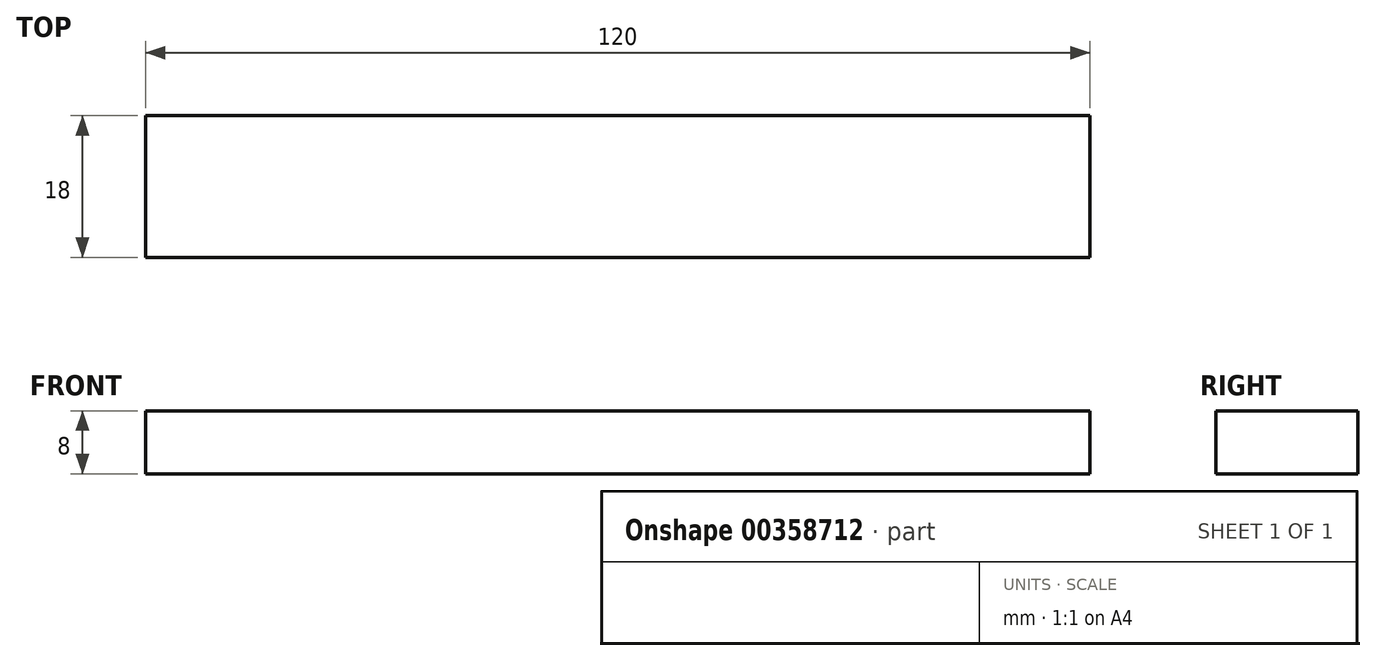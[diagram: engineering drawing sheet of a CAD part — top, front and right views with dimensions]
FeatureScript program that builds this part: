
annotation { "Feature Type Name" : "Feature", "Feature Type Description" : "" }
export const myFeature = defineFeature(function(context is Context, id is Id, definition is map)
    precondition{}
    {
        {
            var Q0;
            Q0=qCreatedBy(makeId("Right.planeOp"),FACE);
            var sketch = newSketch(context, id + "F0", { "sketchPlane" : qUnion([Q0])});
            skLineSegment(sketch, "E0.bottom", {"start": v(9, -4) * mm, "end": v(-9, -4) * mm});
            skLineSegment(sketch, "E0.top", {"start": v(9, 4) * mm, "end": v(-9, 4) * mm});
            skLineSegment(sketch, "E0.left", {"start": v(9, -4) * mm, "end": v(9, 4) * mm});
            skLineSegment(sketch, "E0.right", {"start": v(-9, -4) * mm, "end": v(-9, 4) * mm});
            skPoint(sketch, "E0.middle", {"position": v(0, 0) * mm});
            skSolve(sketch);
        }
        {
            var Q0;
            Q0 = qSketchRegion(id + "F0", true);
            extrude(context, id + "F1", {"entities" : qUnion([Q0]), "depth" : 120 * mm});
        }
    });
